# Revit family: Sink-Vessel-Lavatory-KOHLER-Forefront-K-2660X
name_source: partatom
category: Plumbing Fixtures
units: mm (PartAtom-declared; Revit-internal decimal feet)

## family parameters
Cut with Voids When Loaded = No
Host = Face
OmniClass Number = 23.31.13.00
OmniClass Title = Sinks
Part Type = Normal
Room Calculation Point = No
Round Connector Dimension = Use Diameter
Shared = No

## types (3) — shared parameters
ADA Compliant = No
Assembly Code = D2010400
CW Connection = No
Cold Water Inlet = Cold Water Inlet
Date Modified = 09/05/2023
Default Elevation = 36"
Drain Included = No
HW Connection = No
Height = 6 13/16"
Hot Water Inlet = Hot Water Inlet
Length = 23"
Manufacturer = Kohler Co.
Master Format 2014 = 22 41 16
Master Format 2014 Name = Residential Lavatories and Sinks
Material = Vitreous China
Product Documentation Link = http://resources.kohler.com
Product Name = Forefront
URL = https://www.kohler.co.th
https://www.kohler.co.th
Vent Connection = No
Waste Connection = Yes
Waste Water Outlet = Waste Water Outlet
WaterSense Certified = No
Width = 18 1/8"

## per-type parameters (varying)
| type | 8 inch Faucet Hole | Description | Finish | Model | Product Page URL | Single Faucet Hole | Type |
| Single Faucet Hole, 0-White | No | Rectangular Vessel Lavatory With Faucet Deck With Single Faucet Hole | Kohler-Vitreous_China-0-White | K-2660X-1-0 | https://www.kohler.co.th | Yes | 3 |
| 8 Inch Faucet Hole, 0-White | Yes | Rectangular Vessel Lavatory With Faucet Deck With 8 Inch Widespread Faucet Holes | Kohler-Vitreous_China-0-White | K-2660X-8-0 | https://www.kohler.co.th | No | 1 |
| 8 Inch Faucet Hole, HP1-Peacock | Yes | Rectangular Vessel Lavatory With Faucet Deck With 8 Inch Widespread Faucet Holes | KOHLER-Vitreous_China-HP1-Peacock | K-2660X-8-HP1 |  | No | 2 |

## geometry (parser evidence)
native form markers: Sweep x5
no freeform markers — native parametric forms only
